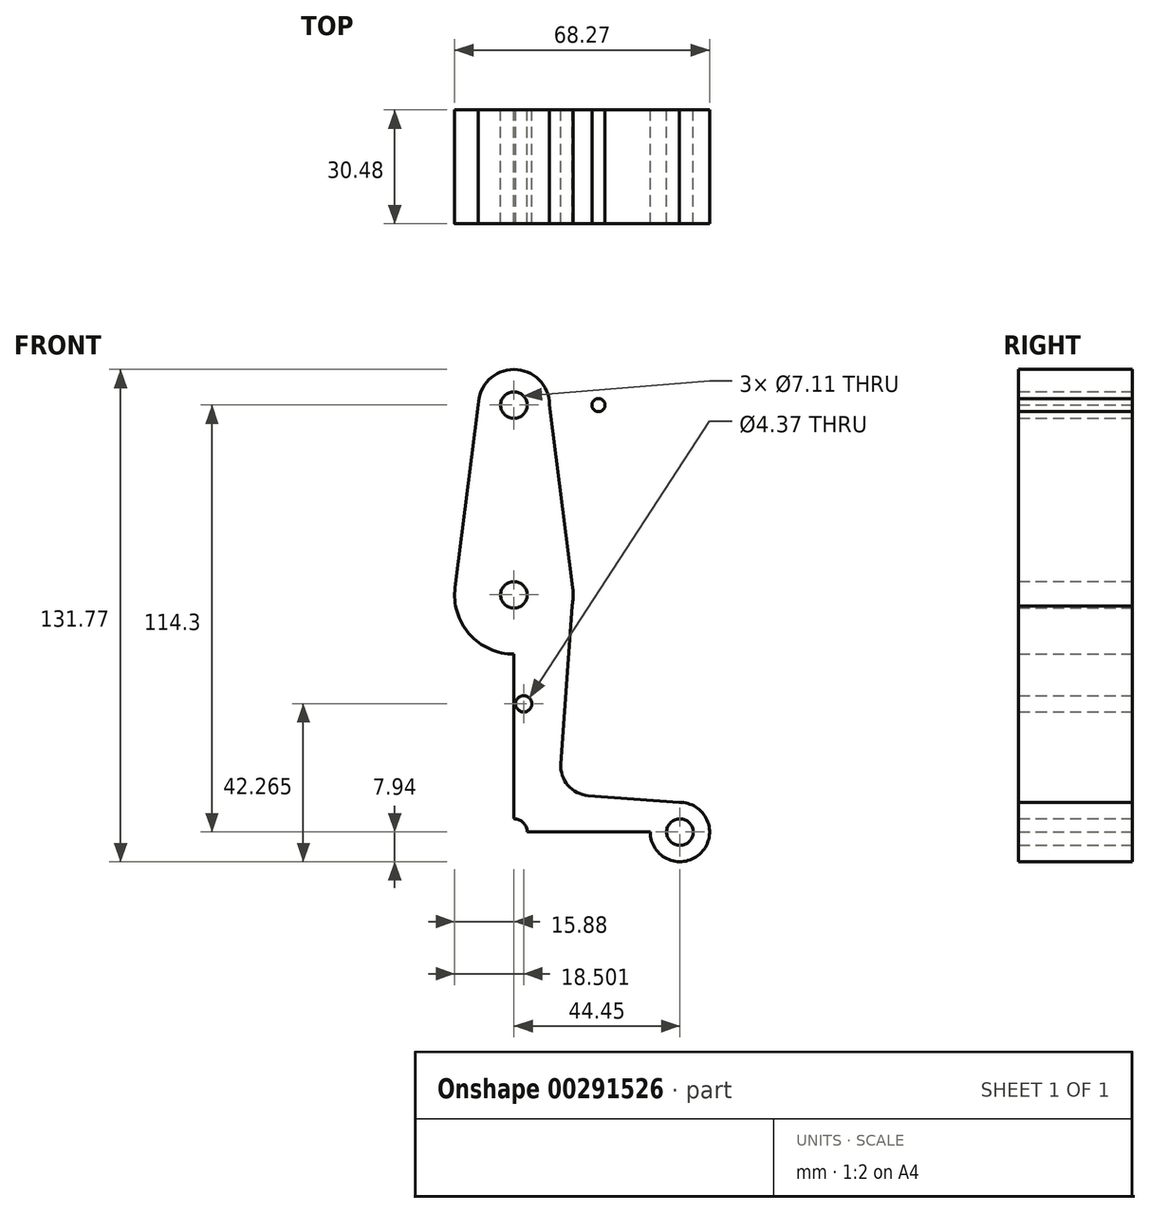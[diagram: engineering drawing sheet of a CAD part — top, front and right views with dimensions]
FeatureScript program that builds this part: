
annotation { "Feature Type Name" : "Feature", "Feature Type Description" : "" }
export const myFeature = defineFeature(function(context is Context, id is Id, definition is map)
    precondition{}
    {
        {
            var Q0;
            Q0=qCreatedBy(makeId("Front.planeOp"),FACE);
            var sketch = newSketch(context, id + "F0", { "sketchPlane" : qUnion([Q0])});
            skLineSegment(sketch, "E0", {"start": v(0, 114.3) * mm, "end": v(0, 0) * mm});
            skLineSegment(sketch, "E1", {"start": v(0, 0) * mm, "end": v(44.45, 0) * mm});
            skCircle(sketch, "E2", {"center": v(0, 0) * mm, "radius": 11.23 * mm});
            skCircle(sketch, "E3", {"center": v(0, 114.3) * mm, "radius": 9.53 * mm});
            skCircle(sketch, "E4", {"center": v(0, 63.5) * mm, "radius": 15.88 * mm});
            skCircle(sketch, "E5", {"center": v(44.45, 0) * mm, "radius": 7.94 * mm});
            skLineSegment(sketch, "E6", {"start": v(-9.52, 114.4) * mm, "end": v(-15.75, 65.5) * mm});
            skLineSegment(sketch, "E7", {"start": v(-15.6, 60.55) * mm, "end": v(-11.26, 0) * mm});
            skLineSegment(sketch, "E8.MirrorCS", {"start": v(9.52, 114.4) * mm, "end": v(15.75, 65.5) * mm});
            skLineSegment(sketch, "E9.MirrorCS", {"start": v(15.6, 60.55) * mm, "end": v(12.57, 18.24) * mm});
            skLineSegment(sketch, "E10", {"start": v(19.9, 9.75) * mm, "end": v(44.24, 7.93) * mm});
            skLineSegment(sketch, "E11", {"start": v(-0.02, -11.21) * mm, "end": v(44.55, -8.04) * mm});
            skPoint(sketch, "E12.newPointA", {"position": v(11.26, 0) * mm});
            skArc(sketch, "E12.filletArc", {"start": v(12.57, 18.24) * mm, "mid": v(14.48, 12.48) * mm, "end": v(19.9, 9.75) * mm});
            skCircle(sketch, "E13", {"center": v(0, 114.3) * mm, "radius": 3.56 * mm});
            skCircle(sketch, "E14", {"center": v(22.65, 114.3) * mm, "radius": 1.76 * mm});
            skCircle(sketch, "E15", {"center": v(0, 63.5) * mm, "radius": 3.56 * mm});
            skCircle(sketch, "E16", {"center": v(0, 0) * mm, "radius": 3.56 * mm});
            skCircle(sketch, "E17", {"center": v(44.45, 0) * mm, "radius": 3.56 * mm});
            skCircle(sketch, "E18", {"center": v(2.62, 34.33) * mm, "radius": 2.18 * mm});
            skSolve(sketch);
        }
        {
            var Q0;
            Q0=makeQuery(id+"F0.imprint","IMPRINT",FACE,{"disambiguationData":[TD([[makeQuery(id+"F0.imprint","IMPRINT",EDGE,{"derivedFrom":sQuery(id+"F0.wireOp",EDGE,"E14")}),1.0]])]});
            var Q1;
            Q1=makeQuery(id+"F0.imprint","IMPRINT",FACE,{"disambiguationData":[TD([[makeQuery(id+"F0.imprint","IMPRINT",EDGE,{"derivedFrom":sQuery(id+"F0.wireOp",EDGE,"E17")}),-1.0]])]});
            var Q2;
            {var subQ5=sQuery(id+"F0.wireOp",EDGE,"E6");Q2=makeQuery(id+"F0.imprint","IMPRINT",FACE,{"disambiguationData":[TD([[makeQuery(id+"F0.imprint","IMPRINT",EDGE,{"derivedFrom":subQ5}),1.0]])]});}
            var Q3;
            {var subQ5=sQuery(id+"F0.wireOp",EDGE,"E8.MirrorCS");Q3=makeQuery(id+"F0.imprint","IMPRINT",FACE,{"disambiguationData":[TD([[makeQuery(id+"F0.imprint","IMPRINT",EDGE,{"derivedFrom":subQ5}),-1.0]])]});}
            var Q4;
            {var subQ0=sQuery(id+"F0.wireOp",EDGE,"E4");var subQ2=makeQuery(id+"F0.imprint","IMPRINT",VERTEX,{"derivedFrom":subQ0});Q4=makeQuery(id+"F0.imprint","IMPRINT",FACE,{"disambiguationData":[TD([[makeQuery(id+"F0.imprint","IMPRINT",EDGE,{"disambiguationData":[TD([[subQ2,1.0]])],"derivedFrom":subQ0}),1.0]])]});}
            var Q5;
            {var subQ0=sQuery(id+"F0.wireOp",EDGE,"E2");var subQ1=sQuery(id+"F0.wireOp",EDGE,"E0");var subQ2=makeQuery(id+"F0.imprint","INTERSECT",VERTEX,{"derivedFrom":[subQ1,subQ0]});Q5=makeQuery(id+"F0.imprint","IMPRINT",FACE,{"disambiguationData":[TD([[makeQuery(id+"F0.imprint","IMPRINT",EDGE,{"disambiguationData":[TD([[subQ2,-1.0]])],"derivedFrom":subQ1}),1.0]])]});}
            var Q6;
            Q6=makeQuery(id+"F0.imprint","IMPRINT",FACE,{"disambiguationData":[TD([[makeQuery(id+"F0.imprint","IMPRINT",EDGE,{"derivedFrom":sQuery(id+"F0.wireOp",EDGE,"E13")}),-1.0]])]});
            var Q7;
            {var subQ0=sQuery(id+"F0.wireOp",EDGE,"E4");var subQ2=sQuery(id+"F0.wireOp",EDGE,"E0");var subQ5=makeQuery(id+"F0.imprint","INTERSECT",VERTEX,{"disambiguationData":[OD(1.0)],"derivedFrom":[subQ2,subQ0]});Q7=makeQuery(id+"F0.imprint","IMPRINT",FACE,{"disambiguationData":[TD([[makeQuery(id+"F0.imprint","IMPRINT",EDGE,{"disambiguationData":[TD([[subQ5,-1.0]])],"derivedFrom":subQ2}),1.0]])]});}
            var Q8;
            {var subQ8=sQuery(id+"F0.wireOp",EDGE,"E9.MirrorCS");Q8=makeQuery(id+"F0.imprint","IMPRINT",FACE,{"disambiguationData":[TD([[makeQuery(id+"F0.imprint","IMPRINT",EDGE,{"derivedFrom":subQ8}),-1.0]])]});}
            extrude(context, id + "F1", {"entities" : qUnion([Q0, Q1, Q2, Q3, Q4, Q5, Q6, Q7, Q8]), "depth" : 30.48 * mm});
        }
    });
